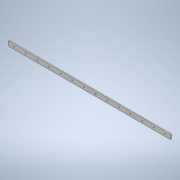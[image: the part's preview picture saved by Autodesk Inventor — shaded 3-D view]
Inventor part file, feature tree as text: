
AUTODESK INVENTOR PART (.ipt)
format: ipt  version: 2022 (Build 260153000, 153)  size: 127,488 bytes
history: native  units: mm
features: sketch x2, extrude x1, hole x1, pattern_linear x1, fillet x1
ambient origin geometry x8: Origin, YZ Plane, XZ Plane, XY Plane, X Axis, Y Axis, Z Axis, Center Point
bodies: Solid1 (feature_tree)
feature tree (6):
  extrude  "Extrusion1"  Depth=10.0mm
  hole  "Hole1"  [1 undecoded]
  pattern_linear  "Rectangular Pattern1"  Count1=14 Spacing1=25.0mm
  fillet  "Fillet1"  Radius=2.0mm
  sketch  "Sketch1"  dims[d0=350.0mm d1=10.0mm]
  sketch  "Sketch2"  dims[d2=2.0mm d3=0.0mm d4=13.0mm d5=2.459mm d6=6.0mm d7=4.0mm d8=2.0mm d9=90.0deg d10=8.0mm d11=20.594885mm d12=140.0mm d14=25.0mm d15=2.0mm]
note: 1 required parameter value undecoded (feature->parameter linkage not recoverable at this tier; creation-order binding heuristic only, values carry confidence <= 0.55)
